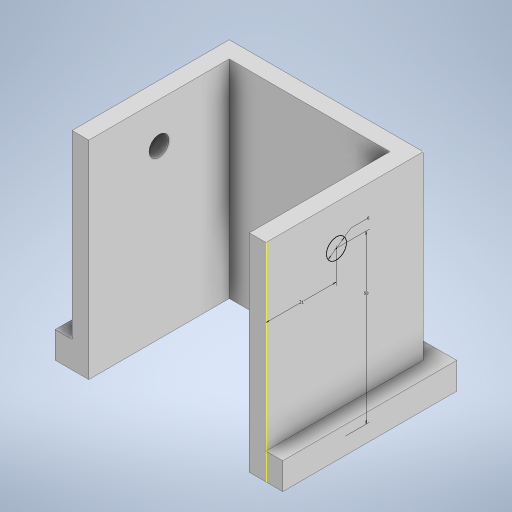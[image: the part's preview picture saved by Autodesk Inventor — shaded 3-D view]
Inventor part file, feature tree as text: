
AUTODESK INVENTOR PART (.ipt)
format: ipt  version: 2023 (Build 270158000, 158)  size: 257,024 bytes
history: native  units: in
note: dims shown in document units (in); Inventor stores cm internally (conversion verified against a paired STEP export)
features: sketch x5, extrude x4
ambient origin geometry x8: Origin, YZ Plane, XZ Plane, XY Plane, X Axis, Y Axis, Z Axis, Center Point
bodies: Solid1 (feature_tree)
feature tree (9):
  extrude  "Extrusion1"  Depth=0.1969in
  sketch  "Sketch2"  dims[d2=0.1969in d3=1.6535in]
  extrude  "Extrusion3"  Depth=1.6535in
  sketch  "Sketch4"  dims[d6=2.4409in d7=0.0in d8=0.8268in]
  extrude  "Extrusion5"  Depth=1.6535in
  extrude  "Extrusion6"  Depth=2.4409in
  sketch  "Sketch1"  dims[d0=2.2835in d1=0.1969in]
  sketch  "Sketch3"  dims[d4=0.1969in d5=1.6535in]
  sketch  "Sketch5"  dims[d9=1.9685in d10=0.2362in d13=0.1969in d14=0.1969in d15=0.1969in d16=0.315in d17=0.0in d18=0.3937in d19=0.3937in d20=0.1969in d21=0.1969in d25=0.1969in d26=0.0in d29=0.1969in d30=0.1969in d31=0.1969in d32=0.0in d11=0.0197in d12=0.0344in]
